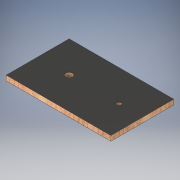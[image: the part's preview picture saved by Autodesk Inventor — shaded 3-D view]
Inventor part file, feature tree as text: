
AUTODESK INVENTOR PART (.ipt)
format: ipt  version: 2017 (Build 210142000, 142)  size: 131,072 bytes
history: native  units: in
note: dims shown in document units (in); Inventor stores cm internally (conversion verified against a paired STEP export)
features: extrude x2, sketch x2
ambient origin geometry x8: Origin, YZ Plane, XZ Plane, XY Plane, X Axis, Y Axis, Z Axis, Center Point
bodies: Solid1 (feature_tree)
feature tree (4):
  extrude  "Extrusion1"  Depth=0.4688in TaperAngle=0.0deg
  extrude  "Extrusion2"  Depth=0.4688in
  sketch  "Sketch1"  dims[d0=6.0in d1=9.9688in d2=2.2188in d3=0.375in d4=0.4688in d5=0.0in]
  sketch  "Sketch2"  dims[d6=6.9688in d7=0.625in d8=0.4688in d9=0.0in]
